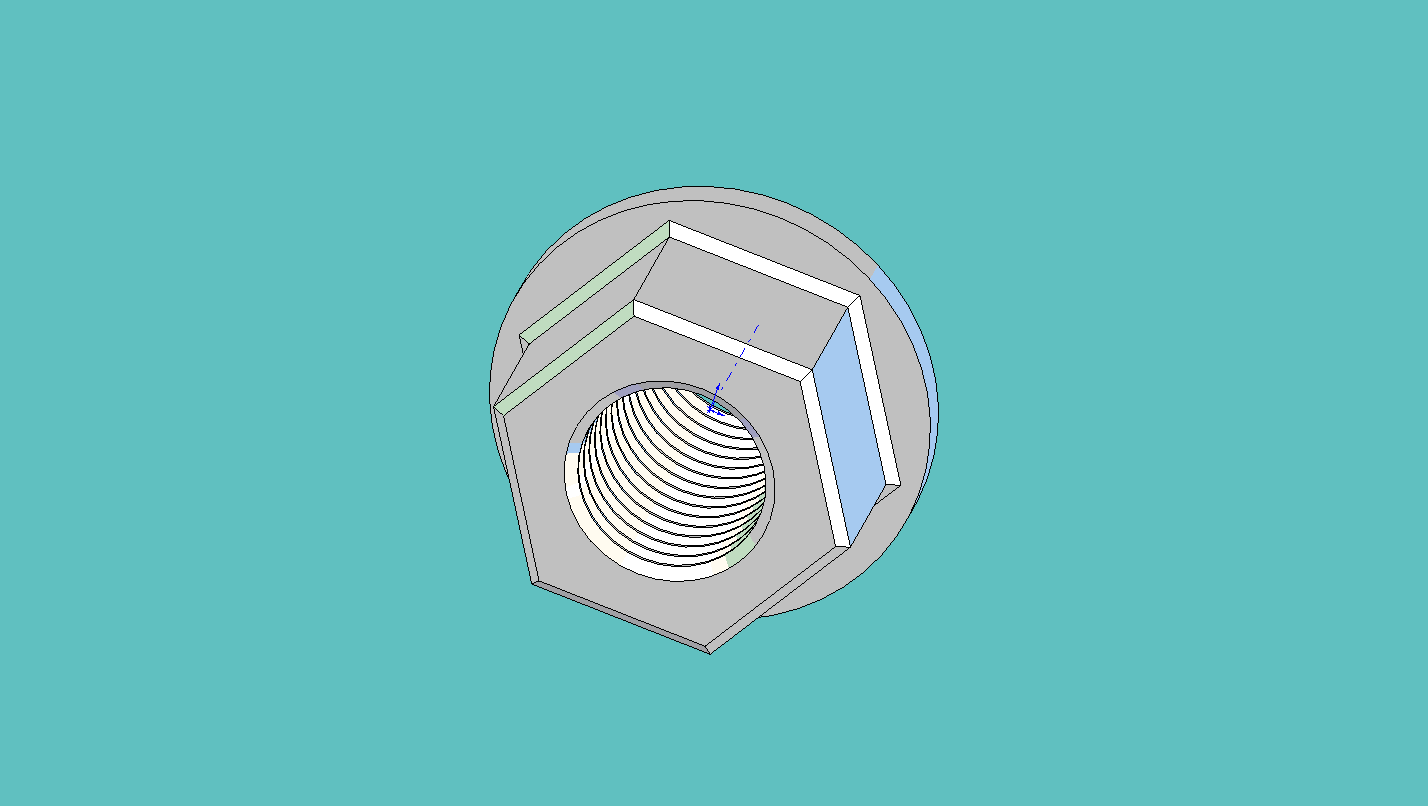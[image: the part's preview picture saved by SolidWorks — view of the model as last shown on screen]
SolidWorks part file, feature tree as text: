
SOLIDWORKS PART (.sldprt)
format: sldprt  version: not decoded by parser v0  size: 263,168 bytes
history: native  units: mm
features: sketch x6, extrude x3, chamfer x2, material x1, cut_extrude x1, plane x1, cut_revolve x1, pattern_linear x1 (+13 scaffold rows collapsed)
feature tree (29):
  scaffold x13  (default folders/planes/origin — collapsed)
  material  "Material <not specified>"
  sketch  "Sketch2"
  extrude  "Extrude1"  Depth=12.7mm
  sketch  "Sketch3"
  extrude  "Extrude2"  Depth=2.54mm
  chamfer  "Chamfer1"  Distance=0.762mm Angle=45deg
  chamfer  "Chamfer2"  Distance=0.762mm Angle=45deg
  sketch  "Sketch5"
  extrude  "Extrude3"  Depth=12.7mm
  sketch  "Sketch4"  dims[D1=12.7mm]
  cut_extrude  "Cut-Extrude1"  [1 undecoded]
  plane  "Plane1"  Offset=2.54mm
  sketch  "Sketch6"  dims[D1=11.43mm]
  sketch  "Sketch7"  dims[D1=1.524mm D2=1.524mm D3=~5.176223mm]
  cut_revolve  "Cut-Revolve1"  Angle=360deg
  pattern_linear  "LPattern2"  Count1=17 Count2=1 Spacing1=1.74mm Spacing2=50mm
decode coverage: 10 of 14 modeling features carry decoded parameters
note: ~ marks probable driven/reference dimensions
note: 1 parameter value undecoded
note: suppression state not decoded; provenance and decode notes live in map.json
